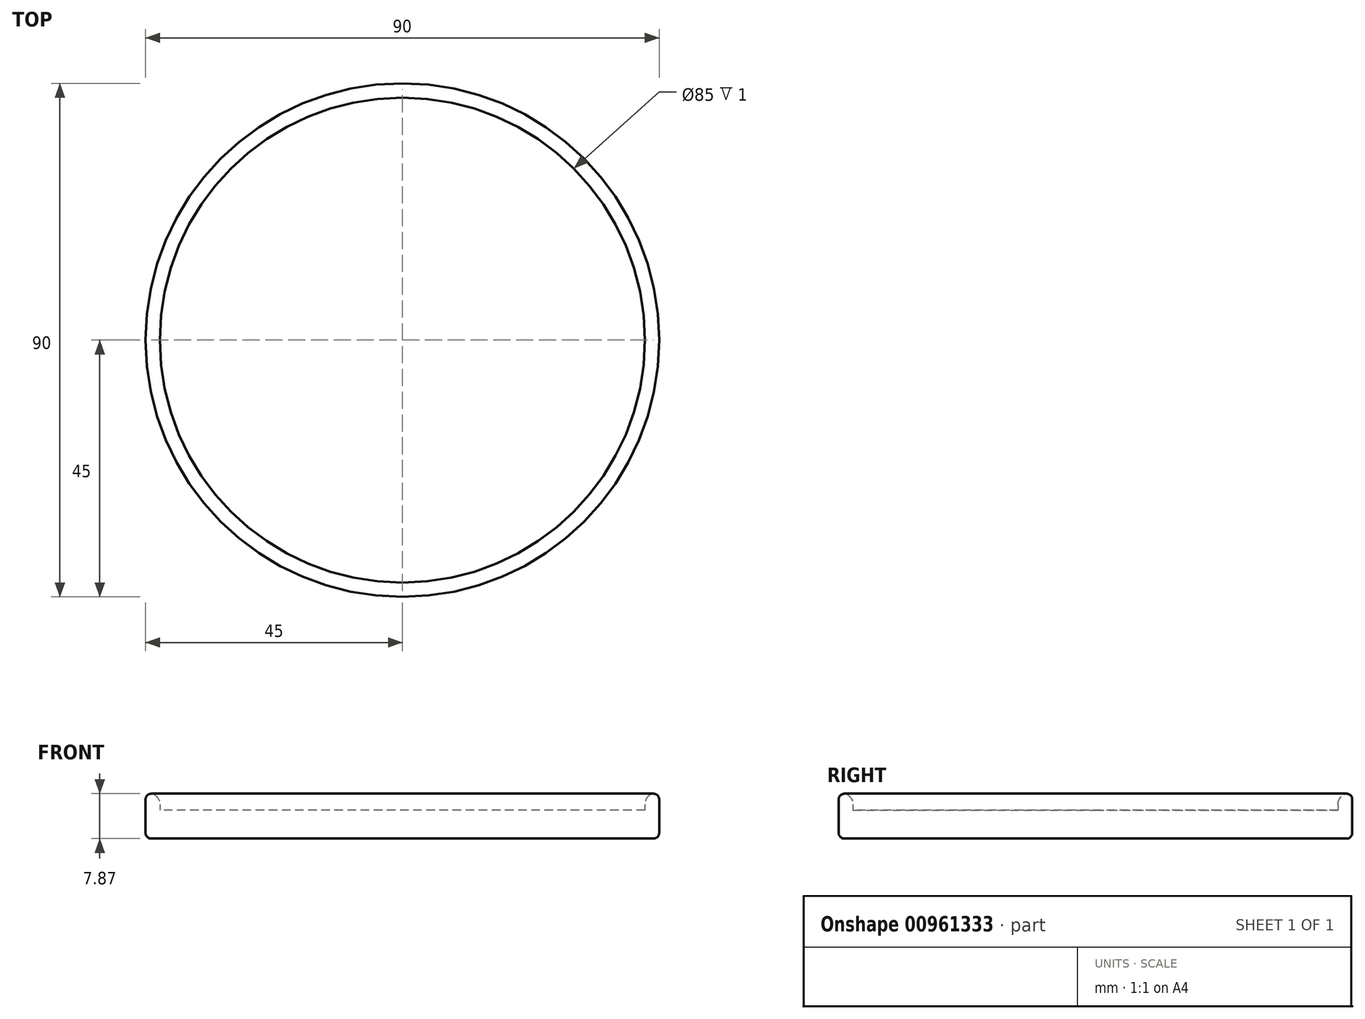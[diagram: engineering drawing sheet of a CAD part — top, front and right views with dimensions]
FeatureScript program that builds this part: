
annotation { "Feature Type Name" : "Feature", "Feature Type Description" : "" }
export const myFeature = defineFeature(function(context is Context, id is Id, definition is map)
    precondition{}
    {
        {
            var Q0;
            Q0=qCreatedBy(makeId("Top.planeOp"),FACE);
            var sketch = newSketch(context, id + "F0", { "sketchPlane" : qUnion([Q0])});
            skCircle(sketch, "E0", {"center": v(0, 0) * mm, "radius": 45 * mm});
            skCircle(sketch, "E1", {"center": v(0, 0) * mm, "radius": 42.5 * mm});
            skSolve(sketch);
        }
        {
            var Q0;
            Q0=makeQuery(id+"F0.imprint","IMPRINT",FACE,{"disambiguationData":[TD([[makeQuery(id+"F0.imprint","IMPRINT",EDGE,{"derivedFrom":sQuery(id+"F0.wireOp",EDGE,"E1")}),1.0]])]});
            extrude(context, id + "F1", {"entities" : qUnion([Q0]), "depth" : 5 * mm, "offsetDistance" : 25 * mm});
        }
        {
            var Q0;
            Q0=makeQuery(id+"F0.imprint","IMPRINT",FACE,{"disambiguationData":[TD([[makeQuery(id+"F0.imprint","IMPRINT",EDGE,{"derivedFrom":sQuery(id+"F0.wireOp",EDGE,"E0")}),1.0]])]});
            extrude(context, id + "F2", {"entities" : qUnion([Q0]), "operationType" : NewBodyOperationType.ADD, "depth" : 8 * mm, "offsetDistance" : 25 * mm});
        }
        {
            var Q0;
            Q0=makeQuery(id+"F2.opExtrude","CAP_EDGE",EDGE,{"disambiguationData":[OSD([sQuery(id+"F0.wireOp",EDGE,"E1")])],"isStart":false});
            fillet(context, id + "F3", {"entities" : qUnion([Q0]), "radius" : 2 * mm, "allowEdgeOverflow" : false});
        }
        {
            var Q0;
            Q0=makeQuery(id+"F2.opExtrude","SWEPT_FACE",FACE,{"disambiguationData":[OSD([sQuery(id+"F0.wireOp",EDGE,"E0")])]});
            fillet(context, id + "F4", {"entities" : qUnion([Q0]), "radius" : 1 * mm, "tangentPropagation" : true, "allowEdgeOverflow" : false});
        }
    });
